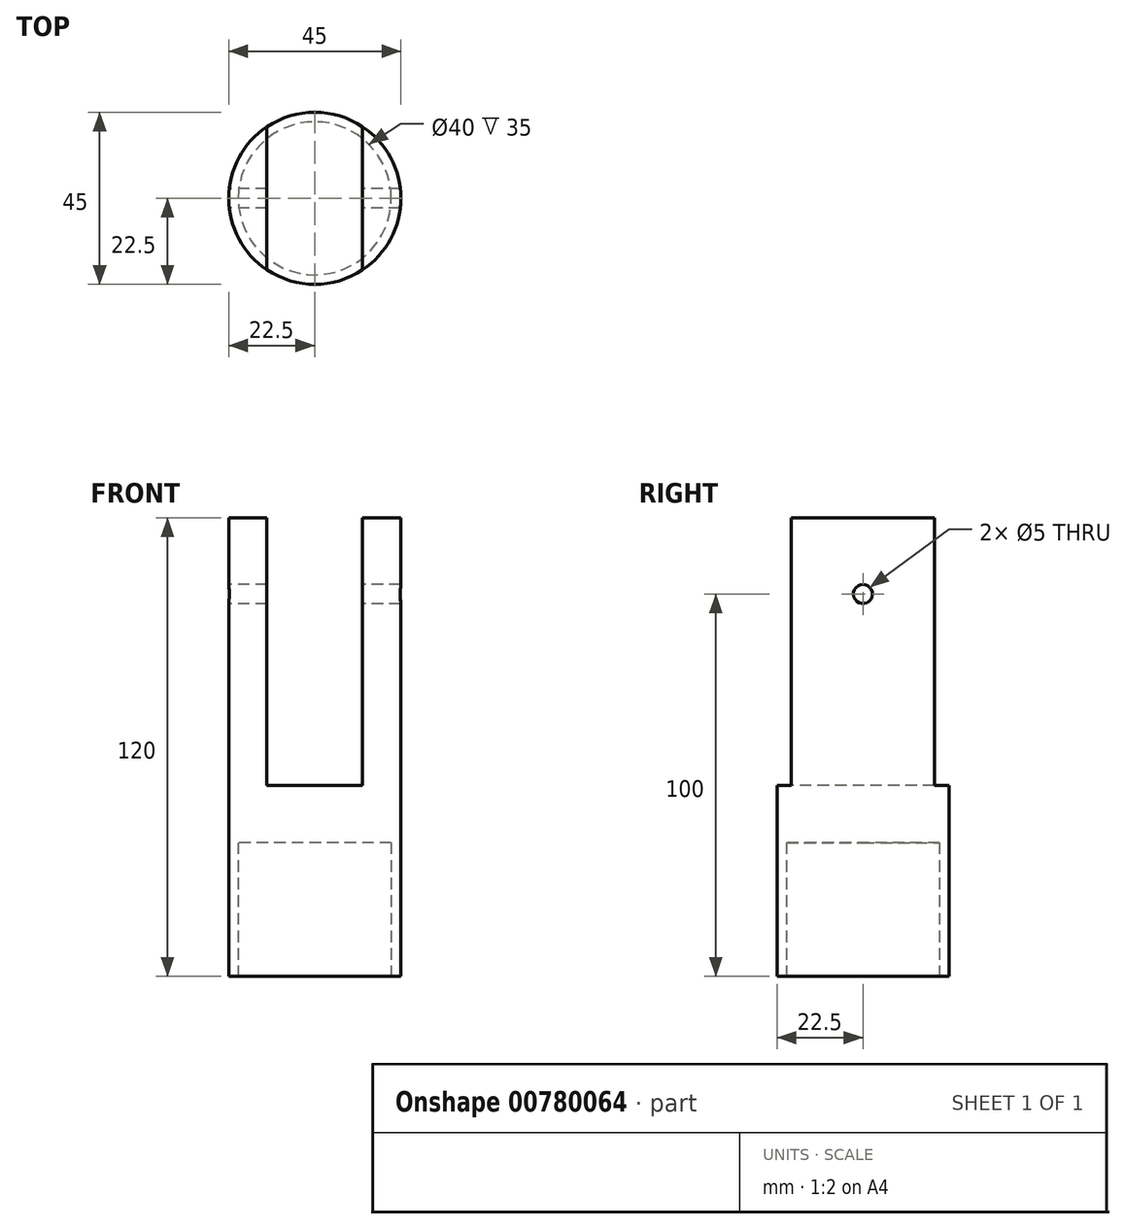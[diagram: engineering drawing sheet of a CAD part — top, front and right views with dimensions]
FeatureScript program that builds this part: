
annotation { "Feature Type Name" : "Feature", "Feature Type Description" : "" }
export const myFeature = defineFeature(function(context is Context, id is Id, definition is map)
    precondition{}
    {
        {
            var Q0;
            Q0=qCreatedBy(makeId("Top.planeOp"),FACE);
            var sketch = newSketch(context, id + "F0", { "sketchPlane" : qUnion([Q0])});
            skCircle(sketch, "E0", {"center": v(0, 0) * mm, "radius": 22.5 * mm});
            skSolve(sketch);
        }
        {
            var Q0;
            Q0 = qSketchRegion(id + "F0", true);
            extrude(context, id + "F1", {"entities" : qUnion([Q0]), "depth" : 120 * mm, "offsetDistance" : 25 * mm});
        }
        {
            var Q0;
            Q0=makeQuery(id+"F1.opExtrude","CAP_FACE",FACE,{"disambiguationData":[OSD([sQuery(id+"F0.wireOp",EDGE,"E0")])],"isStart":false});
            var sketch = newSketch(context, id + "F2", { "sketchPlane" : qUnion([Q0])});
            skLineSegment(sketch, "E1", {"start": v(-12.5, 18.7) * mm, "end": v(-12.5, -18.7) * mm});
            skLineSegment(sketch, "E2", {"start": v(12.5, 18.7) * mm, "end": v(12.5, -18.7) * mm});
            skSolve(sketch);
        }
        {
            var Q0;
            {var subQ0=sQuery(id+"F2.wireOp",EDGE,"E1");Q0=makeQuery(id+"F2.imprint","IMPRINT",FACE,{"disambiguationData":[TD([[makeQuery(id+"F2.imprint","IMPRINT",EDGE,{"derivedFrom":subQ0}),1.0]])]});}
            extrude(context, id + "F3", {"entities" : qUnion([Q0]), "operationType" : NewBodyOperationType.REMOVE, "oppositeDirection" : true, "depth" : 70 * mm, "offsetDistance" : 25 * mm});
        }
        {
            var Q0;
            Q0=qCreatedBy(makeId("Top.planeOp"),FACE);
            var sketch = newSketch(context, id + "F4", { "sketchPlane" : qUnion([Q0])});
            skCircle(sketch, "E3", {"center": v(0, 0) * mm, "radius": 20 * mm});
            skSolve(sketch);
        }
        {
            var Q0;
            Q0 = qSketchRegion(id + "F4", true);
            extrude(context, id + "F5", {"entities" : qUnion([Q0]), "operationType" : NewBodyOperationType.REMOVE, "depth" : 35 * mm, "offsetDistance" : 25 * mm});
        }
        {
            var Q0;
            Q0=qCreatedBy(makeId("Right.planeOp"),FACE);
            var sketch = newSketch(context, id + "F6", { "sketchPlane" : qUnion([Q0])});
            skCircle(sketch, "E4", {"center": v(0, 100) * mm, "radius": 2.5 * mm});
            skSolve(sketch);
        }
        {
            var Q0;
            Q0 = qSketchRegion(id + "F6", true);
            extrude(context, id + "F7", {"entities" : qUnion([Q0]), "operationType" : NewBodyOperationType.REMOVE, "endBound" : BoundingType.SYMMETRIC, "depth" : 100 * mm, "offsetDistance" : 25 * mm});
        }
    });
